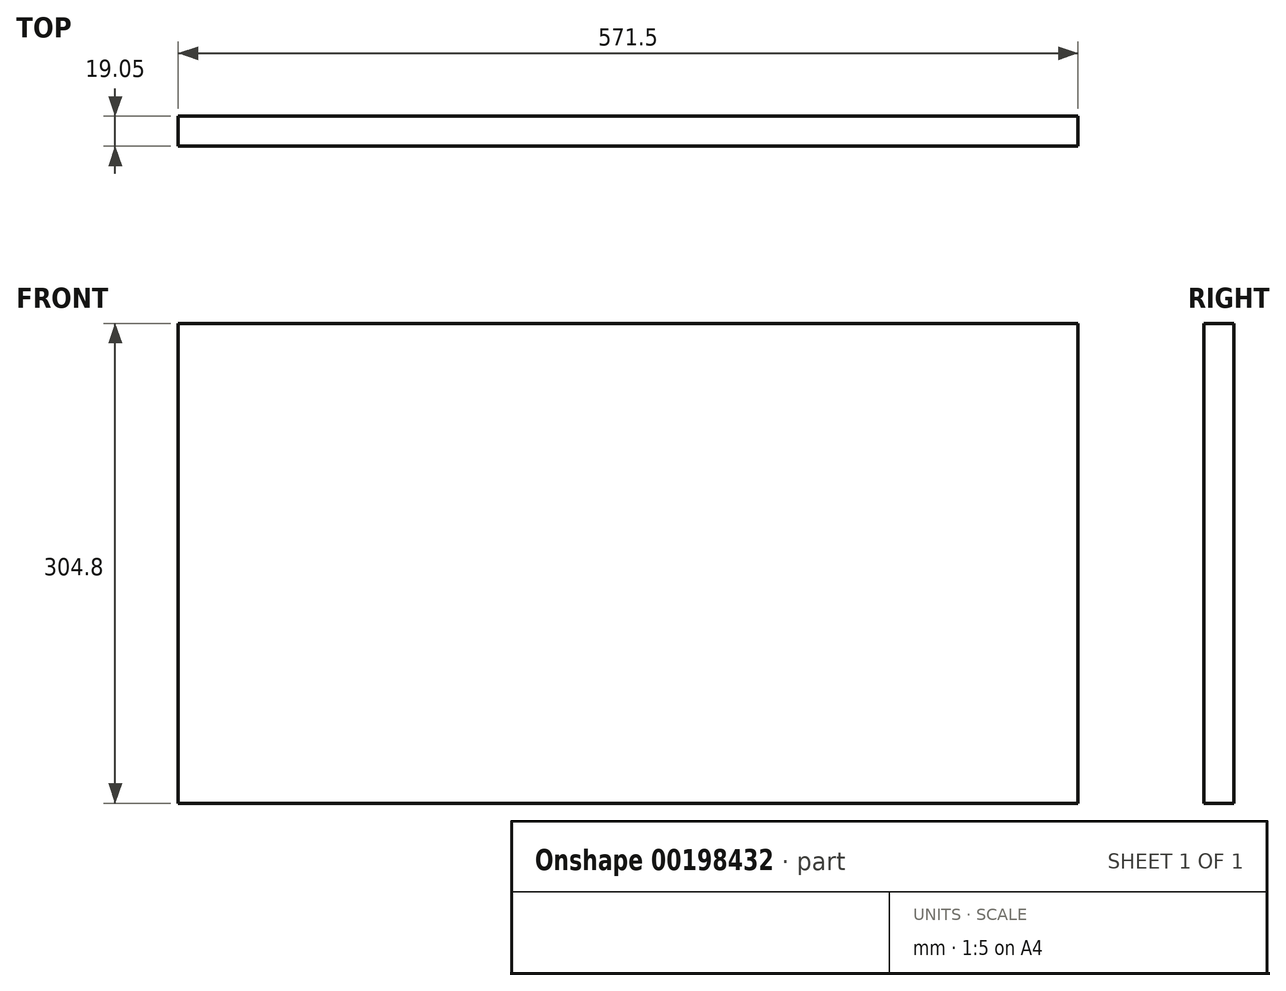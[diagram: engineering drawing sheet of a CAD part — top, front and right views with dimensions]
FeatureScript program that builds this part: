
annotation { "Feature Type Name" : "Feature", "Feature Type Description" : "" }
export const myFeature = defineFeature(function(context is Context, id is Id, definition is map)
    precondition{}
    {
        {
            var Q0;
            Q0=qCreatedBy(makeId("Front.planeOp"),FACE);
            var sketch = newSketch(context, id + "F0", { "sketchPlane" : qUnion([Q0])});
            skLineSegment(sketch, "E0.bottom", {"start": v(0, 0) * mm, "end": v(571.5, 0) * mm});
            skLineSegment(sketch, "E0.top", {"start": v(0, 304.8) * mm, "end": v(571.5, 304.8) * mm});
            skLineSegment(sketch, "E0.left", {"start": v(0, 0) * mm, "end": v(0, 304.8) * mm});
            skLineSegment(sketch, "E0.right", {"start": v(571.5, 0) * mm, "end": v(571.5, 304.8) * mm});
            skSolve(sketch);
        }
        {
            var Q0;
            Q0=makeQuery(id+"F0.imprint","IMPRINT",FACE,{"disambiguationData":[TD([[makeQuery(id+"F0.imprint","IMPRINT",EDGE,{"derivedFrom":sQuery(id+"F0.wireOp",EDGE,"E0.bottom")}),1.0]])]});
            extrude(context, id + "F1", {"entities" : qUnion([Q0]), "depth" : 19.05 * mm});
        }
    });
